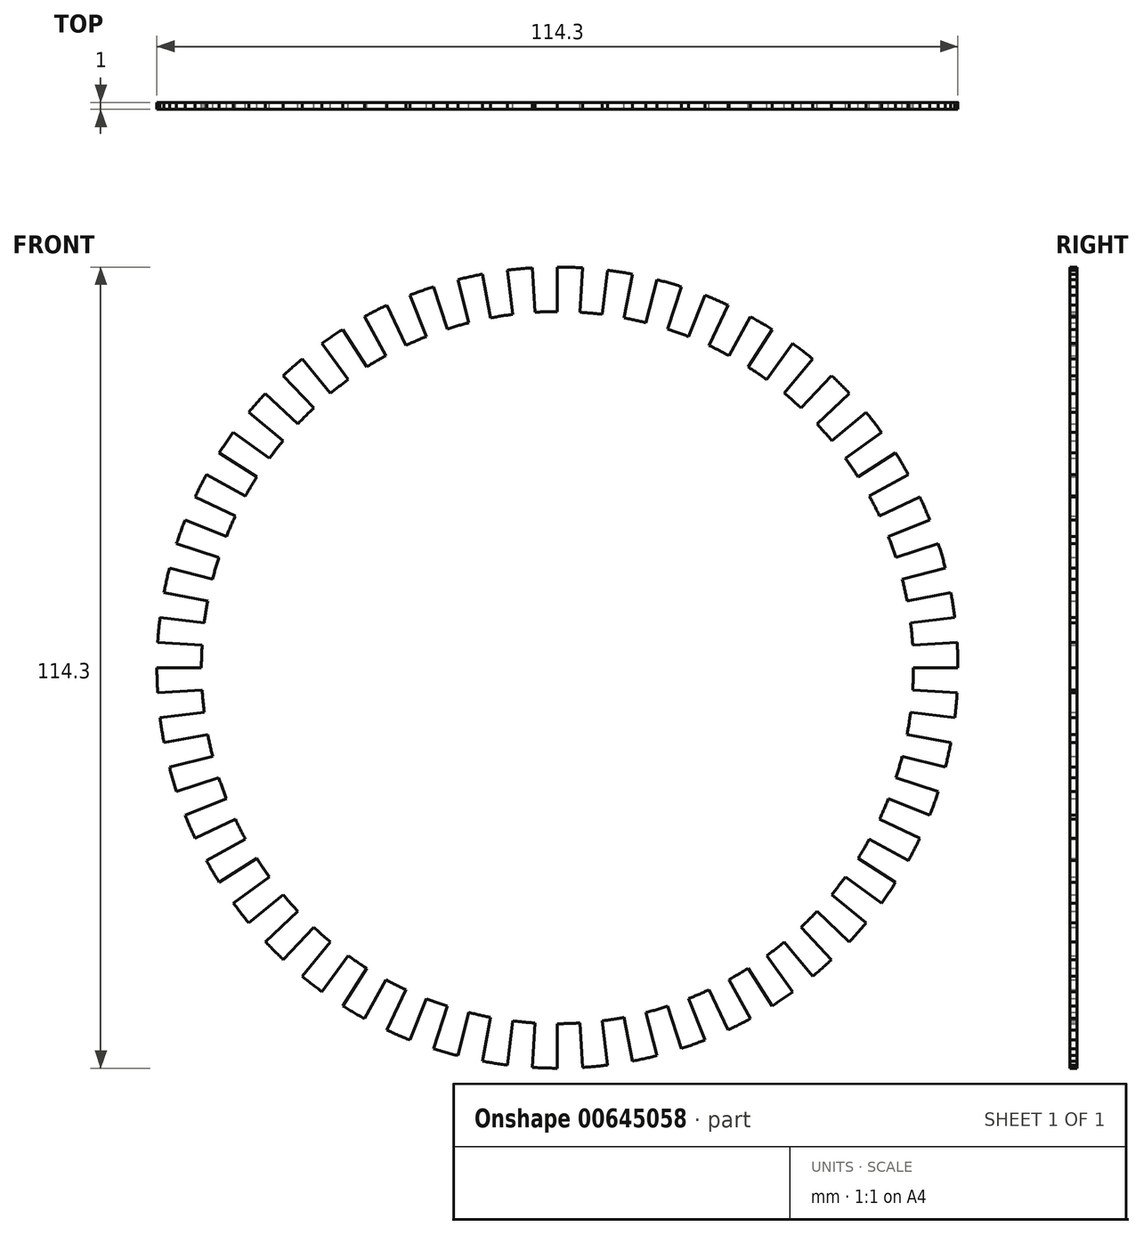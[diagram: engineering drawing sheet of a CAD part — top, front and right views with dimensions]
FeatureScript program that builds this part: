
annotation { "Feature Type Name" : "Feature", "Feature Type Description" : "" }
export const myFeature = defineFeature(function(context is Context, id is Id, definition is map)
    precondition{}
    {
        {
            var Q0;
            Q0=qCreatedBy(makeId("Front.planeOp"),FACE);
            var sketch = newSketch(context, id + "F0", { "sketchPlane" : qUnion([Q0])});
            skCircle(sketch, "E0", {"center": v(0, 0) * mm, "radius": 50.8 * mm});
            skCircle(sketch, "E1", {"center": v(0, 0) * mm, "radius": 57.15 * mm, "construction": true});
            skLineSegment(sketch, "E2", {"start": v(0, 50.8) * mm, "end": v(0, 57.15) * mm});
            skLineSegment(sketch, "E3", {"start": v(3.19, 50.7) * mm, "end": v(3.59, 57.04) * mm});
            skArc(sketch, "E4", {"start": v(0, 57.15) * mm, "mid": v(1.8, 57.12) * mm, "end": v(3.59, 57.04) * mm});
            skLineSegment(sketch, "E5.1.0", {"start": v(-3.19, 50.7) * mm, "end": v(-3.59, 57.04) * mm});
            skArc(sketch, "E5.1.1", {"start": v(-7.16, 56.7) * mm, "mid": v(-5.38, 56.9) * mm, "end": v(-3.59, 57.04) * mm});
            skLineSegment(sketch, "E5.1.2", {"start": v(-6.37, 50.4) * mm, "end": v(-7.16, 56.7) * mm});
            skLineSegment(sketch, "E5.2.0", {"start": v(-9.52, 49.9) * mm, "end": v(-10.7, 56.14) * mm});
            skArc(sketch, "E5.2.1", {"start": v(-14.21, 55.35) * mm, "mid": v(-12.47, 55.77) * mm, "end": v(-10.7, 56.14) * mm});
            skLineSegment(sketch, "E5.2.2", {"start": v(-12.63, 49.2) * mm, "end": v(-14.21, 55.35) * mm});
            skArc(sketch, "E6.3.3.0", {"start": v(-21.04, 53.14) * mm, "mid": v(-19.36, 53.77) * mm, "end": v(-17.66, 54.35) * mm});
            skLineSegment(sketch, "E6.7.3.0", {"start": v(-18.7, 47.23) * mm, "end": v(-21.04, 53.14) * mm});
            skLineSegment(sketch, "E6.8.3.0", {"start": v(-15.7, 48.31) * mm, "end": v(-17.66, 54.35) * mm});
            skArc(sketch, "E6.3.4.0", {"start": v(-27.53, 50.08) * mm, "mid": v(-25.95, 50.92) * mm, "end": v(-24.33, 51.71) * mm});
            skLineSegment(sketch, "E6.7.4.0", {"start": v(-24.47, 44.52) * mm, "end": v(-27.53, 50.08) * mm});
            skLineSegment(sketch, "E6.8.4.0", {"start": v(-21.63, 45.97) * mm, "end": v(-24.33, 51.71) * mm});
            skArc(sketch, "E6.3.5.0", {"start": v(-33.6, 46.24) * mm, "mid": v(-32.12, 47.27) * mm, "end": v(-30.62, 48.25) * mm});
            skLineSegment(sketch, "E6.7.5.0", {"start": v(-29.86, 41.1) * mm, "end": v(-33.6, 46.24) * mm});
            skLineSegment(sketch, "E6.8.5.0", {"start": v(-27.22, 42.9) * mm, "end": v(-30.62, 48.25) * mm});
            skArc(sketch, "E6.3.6.0", {"start": v(-39.12, 41.66) * mm, "mid": v(-37.8, 42.87) * mm, "end": v(-36.43, 44.03) * mm});
            skLineSegment(sketch, "E6.7.6.0", {"start": v(-34.77, 37.03) * mm, "end": v(-39.12, 41.66) * mm});
            skLineSegment(sketch, "E6.8.6.0", {"start": v(-32.38, 39.14) * mm, "end": v(-36.43, 44.03) * mm});
            skArc(sketch, "E6.3.7.0", {"start": v(-44.03, 36.43) * mm, "mid": v(-42.87, 37.8) * mm, "end": v(-41.66, 39.12) * mm});
            skLineSegment(sketch, "E6.7.7.0", {"start": v(-39.14, 32.38) * mm, "end": v(-44.03, 36.43) * mm});
            skLineSegment(sketch, "E6.8.7.0", {"start": v(-37.03, 34.77) * mm, "end": v(-41.66, 39.12) * mm});
            skArc(sketch, "E6.3.8.0", {"start": v(-48.25, 30.62) * mm, "mid": v(-47.27, 32.12) * mm, "end": v(-46.24, 33.6) * mm});
            skLineSegment(sketch, "E6.7.8.0", {"start": v(-42.9, 27.22) * mm, "end": v(-48.25, 30.62) * mm});
            skLineSegment(sketch, "E6.8.8.0", {"start": v(-41.1, 29.86) * mm, "end": v(-46.24, 33.6) * mm});
            skArc(sketch, "E6.3.9.0", {"start": v(-51.71, 24.33) * mm, "mid": v(-50.92, 25.95) * mm, "end": v(-50.08, 27.53) * mm});
            skLineSegment(sketch, "E6.7.9.0", {"start": v(-45.97, 21.63) * mm, "end": v(-51.71, 24.33) * mm});
            skLineSegment(sketch, "E6.8.9.0", {"start": v(-44.52, 24.47) * mm, "end": v(-50.08, 27.53) * mm});
            skArc(sketch, "E6.3.10.0", {"start": v(-54.35, 17.66) * mm, "mid": v(-53.77, 19.36) * mm, "end": v(-53.14, 21.04) * mm});
            skLineSegment(sketch, "E6.7.10.0", {"start": v(-48.31, 15.7) * mm, "end": v(-54.35, 17.66) * mm});
            skLineSegment(sketch, "E6.8.10.0", {"start": v(-47.23, 18.7) * mm, "end": v(-53.14, 21.04) * mm});
            skArc(sketch, "E6.3.11.0", {"start": v(-56.14, 10.7) * mm, "mid": v(-55.77, 12.47) * mm, "end": v(-55.35, 14.21) * mm});
            skLineSegment(sketch, "E6.7.11.0", {"start": v(-49.9, 9.52) * mm, "end": v(-56.14, 10.7) * mm});
            skLineSegment(sketch, "E6.8.11.0", {"start": v(-49.2, 12.63) * mm, "end": v(-55.35, 14.21) * mm});
            skArc(sketch, "E6.3.12.0", {"start": v(-57.04, 3.59) * mm, "mid": v(-56.9, 5.38) * mm, "end": v(-56.7, 7.16) * mm});
            skLineSegment(sketch, "E6.7.12.0", {"start": v(-50.7, 3.19) * mm, "end": v(-57.04, 3.59) * mm});
            skLineSegment(sketch, "E6.8.12.0", {"start": v(-50.4, 6.37) * mm, "end": v(-56.7, 7.16) * mm});
            skArc(sketch, "E6.3.13.0", {"start": v(-57.04, -3.59) * mm, "mid": v(-57.12, -1.8) * mm, "end": v(-57.15, 0) * mm});
            skLineSegment(sketch, "E6.7.13.0", {"start": v(-50.7, -3.19) * mm, "end": v(-57.04, -3.59) * mm});
            skLineSegment(sketch, "E6.8.13.0", {"start": v(-50.8, 0) * mm, "end": v(-57.15, 0) * mm});
            skArc(sketch, "E6.3.14.0", {"start": v(-56.14, -10.7) * mm, "mid": v(-56.45, -8.94) * mm, "end": v(-56.7, -7.16) * mm});
            skLineSegment(sketch, "E6.7.14.0", {"start": v(-49.9, -9.52) * mm, "end": v(-56.14, -10.7) * mm});
            skLineSegment(sketch, "E6.8.14.0", {"start": v(-50.4, -6.37) * mm, "end": v(-56.7, -7.16) * mm});
            skArc(sketch, "E6.3.15.0", {"start": v(-54.35, -17.66) * mm, "mid": v(-54.88, -15.94) * mm, "end": v(-55.35, -14.21) * mm});
            skLineSegment(sketch, "E6.7.15.0", {"start": v(-48.31, -15.7) * mm, "end": v(-54.35, -17.66) * mm});
            skLineSegment(sketch, "E6.8.15.0", {"start": v(-49.2, -12.63) * mm, "end": v(-55.35, -14.21) * mm});
            skArc(sketch, "E6.3.16.0", {"start": v(-51.71, -24.33) * mm, "mid": v(-52.45, -22.7) * mm, "end": v(-53.14, -21.04) * mm});
            skLineSegment(sketch, "E6.7.16.0", {"start": v(-45.97, -21.63) * mm, "end": v(-51.71, -24.33) * mm});
            skLineSegment(sketch, "E6.8.16.0", {"start": v(-47.23, -18.7) * mm, "end": v(-53.14, -21.04) * mm});
            skArc(sketch, "E6.3.17.0", {"start": v(-48.25, -30.62) * mm, "mid": v(-49.2, -29.1) * mm, "end": v(-50.08, -27.53) * mm});
            skLineSegment(sketch, "E6.7.17.0", {"start": v(-42.9, -27.22) * mm, "end": v(-48.25, -30.62) * mm});
            skLineSegment(sketch, "E6.8.17.0", {"start": v(-44.52, -24.47) * mm, "end": v(-50.08, -27.53) * mm});
            skArc(sketch, "E6.3.18.0", {"start": v(-44.03, -36.43) * mm, "mid": v(-45.16, -35.03) * mm, "end": v(-46.24, -33.6) * mm});
            skLineSegment(sketch, "E6.7.18.0", {"start": v(-39.14, -32.38) * mm, "end": v(-44.03, -36.43) * mm});
            skLineSegment(sketch, "E6.8.18.0", {"start": v(-41.1, -29.86) * mm, "end": v(-46.24, -33.6) * mm});
            skArc(sketch, "E6.3.19.0", {"start": v(-39.12, -41.66) * mm, "mid": v(-40.41, -40.41) * mm, "end": v(-41.66, -39.12) * mm});
            skLineSegment(sketch, "E6.7.19.0", {"start": v(-34.77, -37.03) * mm, "end": v(-39.12, -41.66) * mm});
            skLineSegment(sketch, "E6.8.19.0", {"start": v(-37.03, -34.77) * mm, "end": v(-41.66, -39.12) * mm});
            skArc(sketch, "E6.3.20.0", {"start": v(-33.6, -46.24) * mm, "mid": v(-35.03, -45.16) * mm, "end": v(-36.43, -44.03) * mm});
            skLineSegment(sketch, "E6.7.20.0", {"start": v(-29.86, -41.1) * mm, "end": v(-33.6, -46.24) * mm});
            skLineSegment(sketch, "E6.8.20.0", {"start": v(-32.38, -39.14) * mm, "end": v(-36.43, -44.03) * mm});
            skArc(sketch, "E6.3.21.0", {"start": v(-27.53, -50.08) * mm, "mid": v(-29.1, -49.2) * mm, "end": v(-30.62, -48.25) * mm});
            skLineSegment(sketch, "E6.7.21.0", {"start": v(-24.47, -44.52) * mm, "end": v(-27.53, -50.08) * mm});
            skLineSegment(sketch, "E6.8.21.0", {"start": v(-27.22, -42.9) * mm, "end": v(-30.62, -48.25) * mm});
            skArc(sketch, "E6.3.22.0", {"start": v(-21.04, -53.14) * mm, "mid": v(-22.7, -52.45) * mm, "end": v(-24.33, -51.71) * mm});
            skLineSegment(sketch, "E6.7.22.0", {"start": v(-18.7, -47.23) * mm, "end": v(-21.04, -53.14) * mm});
            skLineSegment(sketch, "E6.8.22.0", {"start": v(-21.63, -45.97) * mm, "end": v(-24.33, -51.71) * mm});
            skArc(sketch, "E6.3.23.0", {"start": v(-14.21, -55.35) * mm, "mid": v(-15.94, -54.88) * mm, "end": v(-17.66, -54.35) * mm});
            skLineSegment(sketch, "E6.7.23.0", {"start": v(-12.63, -49.2) * mm, "end": v(-14.21, -55.35) * mm});
            skLineSegment(sketch, "E6.8.23.0", {"start": v(-15.7, -48.31) * mm, "end": v(-17.66, -54.35) * mm});
            skArc(sketch, "E6.3.24.0", {"start": v(-7.16, -56.7) * mm, "mid": v(-8.94, -56.45) * mm, "end": v(-10.7, -56.14) * mm});
            skLineSegment(sketch, "E6.7.24.0", {"start": v(-6.37, -50.4) * mm, "end": v(-7.16, -56.7) * mm});
            skLineSegment(sketch, "E6.8.24.0", {"start": v(-9.52, -49.9) * mm, "end": v(-10.7, -56.14) * mm});
            skArc(sketch, "E6.3.25.0", {"start": v(0, -57.15) * mm, "mid": v(-1.8, -57.12) * mm, "end": v(-3.59, -57.04) * mm});
            skLineSegment(sketch, "E6.7.25.0", {"start": v(0, -50.8) * mm, "end": v(0, -57.15) * mm});
            skLineSegment(sketch, "E6.8.25.0", {"start": v(-3.19, -50.7) * mm, "end": v(-3.59, -57.04) * mm});
            skArc(sketch, "E6.3.26.0", {"start": v(7.16, -56.7) * mm, "mid": v(5.38, -56.9) * mm, "end": v(3.59, -57.04) * mm});
            skLineSegment(sketch, "E6.7.26.0", {"start": v(6.37, -50.4) * mm, "end": v(7.16, -56.7) * mm});
            skLineSegment(sketch, "E6.8.26.0", {"start": v(3.19, -50.7) * mm, "end": v(3.59, -57.04) * mm});
            skArc(sketch, "E6.3.27.0", {"start": v(14.21, -55.35) * mm, "mid": v(12.47, -55.77) * mm, "end": v(10.7, -56.14) * mm});
            skLineSegment(sketch, "E6.7.27.0", {"start": v(12.63, -49.2) * mm, "end": v(14.21, -55.35) * mm});
            skLineSegment(sketch, "E6.8.27.0", {"start": v(9.52, -49.9) * mm, "end": v(10.7, -56.14) * mm});
            skArc(sketch, "E6.3.28.0", {"start": v(21.04, -53.14) * mm, "mid": v(19.36, -53.77) * mm, "end": v(17.66, -54.35) * mm});
            skLineSegment(sketch, "E6.7.28.0", {"start": v(18.7, -47.23) * mm, "end": v(21.04, -53.14) * mm});
            skLineSegment(sketch, "E6.8.28.0", {"start": v(15.7, -48.31) * mm, "end": v(17.66, -54.35) * mm});
            skArc(sketch, "E6.3.29.0", {"start": v(27.53, -50.08) * mm, "mid": v(25.95, -50.92) * mm, "end": v(24.33, -51.71) * mm});
            skLineSegment(sketch, "E6.7.29.0", {"start": v(24.47, -44.52) * mm, "end": v(27.53, -50.08) * mm});
            skLineSegment(sketch, "E6.8.29.0", {"start": v(21.63, -45.97) * mm, "end": v(24.33, -51.71) * mm});
            skArc(sketch, "E6.3.30.0", {"start": v(33.6, -46.24) * mm, "mid": v(32.12, -47.27) * mm, "end": v(30.62, -48.25) * mm});
            skLineSegment(sketch, "E6.7.30.0", {"start": v(29.86, -41.1) * mm, "end": v(33.6, -46.24) * mm});
            skLineSegment(sketch, "E6.8.30.0", {"start": v(27.22, -42.9) * mm, "end": v(30.62, -48.25) * mm});
            skArc(sketch, "E6.3.31.0", {"start": v(39.12, -41.66) * mm, "mid": v(37.8, -42.87) * mm, "end": v(36.43, -44.03) * mm});
            skLineSegment(sketch, "E6.7.31.0", {"start": v(34.77, -37.03) * mm, "end": v(39.12, -41.66) * mm});
            skLineSegment(sketch, "E6.8.31.0", {"start": v(32.38, -39.14) * mm, "end": v(36.43, -44.03) * mm});
            skArc(sketch, "E6.3.32.0", {"start": v(44.03, -36.43) * mm, "mid": v(42.87, -37.8) * mm, "end": v(41.66, -39.12) * mm});
            skLineSegment(sketch, "E6.7.32.0", {"start": v(39.14, -32.38) * mm, "end": v(44.03, -36.43) * mm});
            skLineSegment(sketch, "E6.8.32.0", {"start": v(37.03, -34.77) * mm, "end": v(41.66, -39.12) * mm});
            skArc(sketch, "E6.3.33.0", {"start": v(48.25, -30.62) * mm, "mid": v(47.27, -32.12) * mm, "end": v(46.24, -33.6) * mm});
            skLineSegment(sketch, "E6.7.33.0", {"start": v(42.9, -27.22) * mm, "end": v(48.25, -30.62) * mm});
            skLineSegment(sketch, "E6.8.33.0", {"start": v(41.1, -29.86) * mm, "end": v(46.24, -33.6) * mm});
            skArc(sketch, "E6.3.34.0", {"start": v(51.71, -24.33) * mm, "mid": v(50.92, -25.95) * mm, "end": v(50.08, -27.53) * mm});
            skLineSegment(sketch, "E6.7.34.0", {"start": v(45.97, -21.63) * mm, "end": v(51.71, -24.33) * mm});
            skLineSegment(sketch, "E6.8.34.0", {"start": v(44.52, -24.47) * mm, "end": v(50.08, -27.53) * mm});
            skArc(sketch, "E6.3.35.0", {"start": v(54.35, -17.66) * mm, "mid": v(53.77, -19.36) * mm, "end": v(53.14, -21.04) * mm});
            skLineSegment(sketch, "E6.7.35.0", {"start": v(48.31, -15.7) * mm, "end": v(54.35, -17.66) * mm});
            skLineSegment(sketch, "E6.8.35.0", {"start": v(47.23, -18.7) * mm, "end": v(53.14, -21.04) * mm});
            skArc(sketch, "E6.3.36.0", {"start": v(56.14, -10.7) * mm, "mid": v(55.77, -12.47) * mm, "end": v(55.35, -14.21) * mm});
            skLineSegment(sketch, "E6.7.36.0", {"start": v(49.9, -9.52) * mm, "end": v(56.14, -10.7) * mm});
            skLineSegment(sketch, "E6.8.36.0", {"start": v(49.2, -12.63) * mm, "end": v(55.35, -14.21) * mm});
            skArc(sketch, "E6.3.37.0", {"start": v(57.04, -3.59) * mm, "mid": v(56.9, -5.38) * mm, "end": v(56.7, -7.16) * mm});
            skLineSegment(sketch, "E6.7.37.0", {"start": v(50.7, -3.19) * mm, "end": v(57.04, -3.59) * mm});
            skLineSegment(sketch, "E6.8.37.0", {"start": v(50.4, -6.37) * mm, "end": v(56.7, -7.16) * mm});
            skArc(sketch, "E6.3.38.0", {"start": v(57.04, 3.59) * mm, "mid": v(57.12, 1.8) * mm, "end": v(57.15, 0) * mm});
            skLineSegment(sketch, "E6.7.38.0", {"start": v(50.7, 3.19) * mm, "end": v(57.04, 3.59) * mm});
            skLineSegment(sketch, "E6.8.38.0", {"start": v(50.8, 0) * mm, "end": v(57.15, 0) * mm});
            skArc(sketch, "E6.3.39.0", {"start": v(56.14, 10.7) * mm, "mid": v(56.45, 8.94) * mm, "end": v(56.7, 7.16) * mm});
            skLineSegment(sketch, "E6.7.39.0", {"start": v(49.9, 9.52) * mm, "end": v(56.14, 10.7) * mm});
            skLineSegment(sketch, "E6.8.39.0", {"start": v(50.4, 6.37) * mm, "end": v(56.7, 7.16) * mm});
            skArc(sketch, "E6.3.40.0", {"start": v(54.35, 17.66) * mm, "mid": v(54.88, 15.94) * mm, "end": v(55.35, 14.21) * mm});
            skLineSegment(sketch, "E6.7.40.0", {"start": v(48.31, 15.7) * mm, "end": v(54.35, 17.66) * mm});
            skLineSegment(sketch, "E6.8.40.0", {"start": v(49.2, 12.63) * mm, "end": v(55.35, 14.21) * mm});
            skArc(sketch, "E6.3.41.0", {"start": v(51.71, 24.33) * mm, "mid": v(52.45, 22.7) * mm, "end": v(53.14, 21.04) * mm});
            skLineSegment(sketch, "E6.7.41.0", {"start": v(45.97, 21.63) * mm, "end": v(51.71, 24.33) * mm});
            skLineSegment(sketch, "E6.8.41.0", {"start": v(47.23, 18.7) * mm, "end": v(53.14, 21.04) * mm});
            skArc(sketch, "E6.3.42.0", {"start": v(48.25, 30.62) * mm, "mid": v(49.2, 29.1) * mm, "end": v(50.08, 27.53) * mm});
            skLineSegment(sketch, "E6.7.42.0", {"start": v(42.9, 27.22) * mm, "end": v(48.25, 30.62) * mm});
            skLineSegment(sketch, "E6.8.42.0", {"start": v(44.52, 24.47) * mm, "end": v(50.08, 27.53) * mm});
            skArc(sketch, "E6.3.43.0", {"start": v(44.03, 36.43) * mm, "mid": v(45.16, 35.03) * mm, "end": v(46.24, 33.6) * mm});
            skLineSegment(sketch, "E6.7.43.0", {"start": v(39.14, 32.38) * mm, "end": v(44.03, 36.43) * mm});
            skLineSegment(sketch, "E6.8.43.0", {"start": v(41.1, 29.86) * mm, "end": v(46.24, 33.6) * mm});
            skArc(sketch, "E6.3.44.0", {"start": v(39.12, 41.66) * mm, "mid": v(40.41, 40.41) * mm, "end": v(41.66, 39.12) * mm});
            skLineSegment(sketch, "E6.7.44.0", {"start": v(34.77, 37.03) * mm, "end": v(39.12, 41.66) * mm});
            skLineSegment(sketch, "E6.8.44.0", {"start": v(37.03, 34.77) * mm, "end": v(41.66, 39.12) * mm});
            skArc(sketch, "E6.3.45.0", {"start": v(33.6, 46.24) * mm, "mid": v(35.03, 45.16) * mm, "end": v(36.43, 44.03) * mm});
            skLineSegment(sketch, "E6.7.45.0", {"start": v(29.86, 41.1) * mm, "end": v(33.6, 46.24) * mm});
            skLineSegment(sketch, "E6.8.45.0", {"start": v(32.38, 39.14) * mm, "end": v(36.43, 44.03) * mm});
            skArc(sketch, "E6.3.46.0", {"start": v(27.53, 50.08) * mm, "mid": v(29.1, 49.2) * mm, "end": v(30.62, 48.25) * mm});
            skLineSegment(sketch, "E6.7.46.0", {"start": v(24.47, 44.52) * mm, "end": v(27.53, 50.08) * mm});
            skLineSegment(sketch, "E6.8.46.0", {"start": v(27.22, 42.9) * mm, "end": v(30.62, 48.25) * mm});
            skArc(sketch, "E6.3.47.0", {"start": v(21.04, 53.14) * mm, "mid": v(22.7, 52.45) * mm, "end": v(24.33, 51.71) * mm});
            skLineSegment(sketch, "E6.7.47.0", {"start": v(18.7, 47.23) * mm, "end": v(21.04, 53.14) * mm});
            skLineSegment(sketch, "E6.8.47.0", {"start": v(21.63, 45.97) * mm, "end": v(24.33, 51.71) * mm});
            skArc(sketch, "E6.3.48.0", {"start": v(14.21, 55.35) * mm, "mid": v(15.94, 54.88) * mm, "end": v(17.66, 54.35) * mm});
            skLineSegment(sketch, "E6.7.48.0", {"start": v(12.63, 49.2) * mm, "end": v(14.21, 55.35) * mm});
            skLineSegment(sketch, "E6.8.48.0", {"start": v(15.7, 48.31) * mm, "end": v(17.66, 54.35) * mm});
            skArc(sketch, "E6.3.49.0", {"start": v(7.16, 56.7) * mm, "mid": v(8.94, 56.45) * mm, "end": v(10.7, 56.14) * mm});
            skLineSegment(sketch, "E6.7.49.0", {"start": v(6.37, 50.4) * mm, "end": v(7.16, 56.7) * mm});
            skLineSegment(sketch, "E6.8.49.0", {"start": v(9.52, 49.9) * mm, "end": v(10.7, 56.14) * mm});
            skSolve(sketch);
        }
        {
            var Q0;
            Q0 = qSketchRegion(id + "F0", true);
            extrude(context, id + "F1", {"entities" : qUnion([Q0]), "depth" : 1 * mm, "offsetDistance" : 25.4 * mm});
        }
    });
